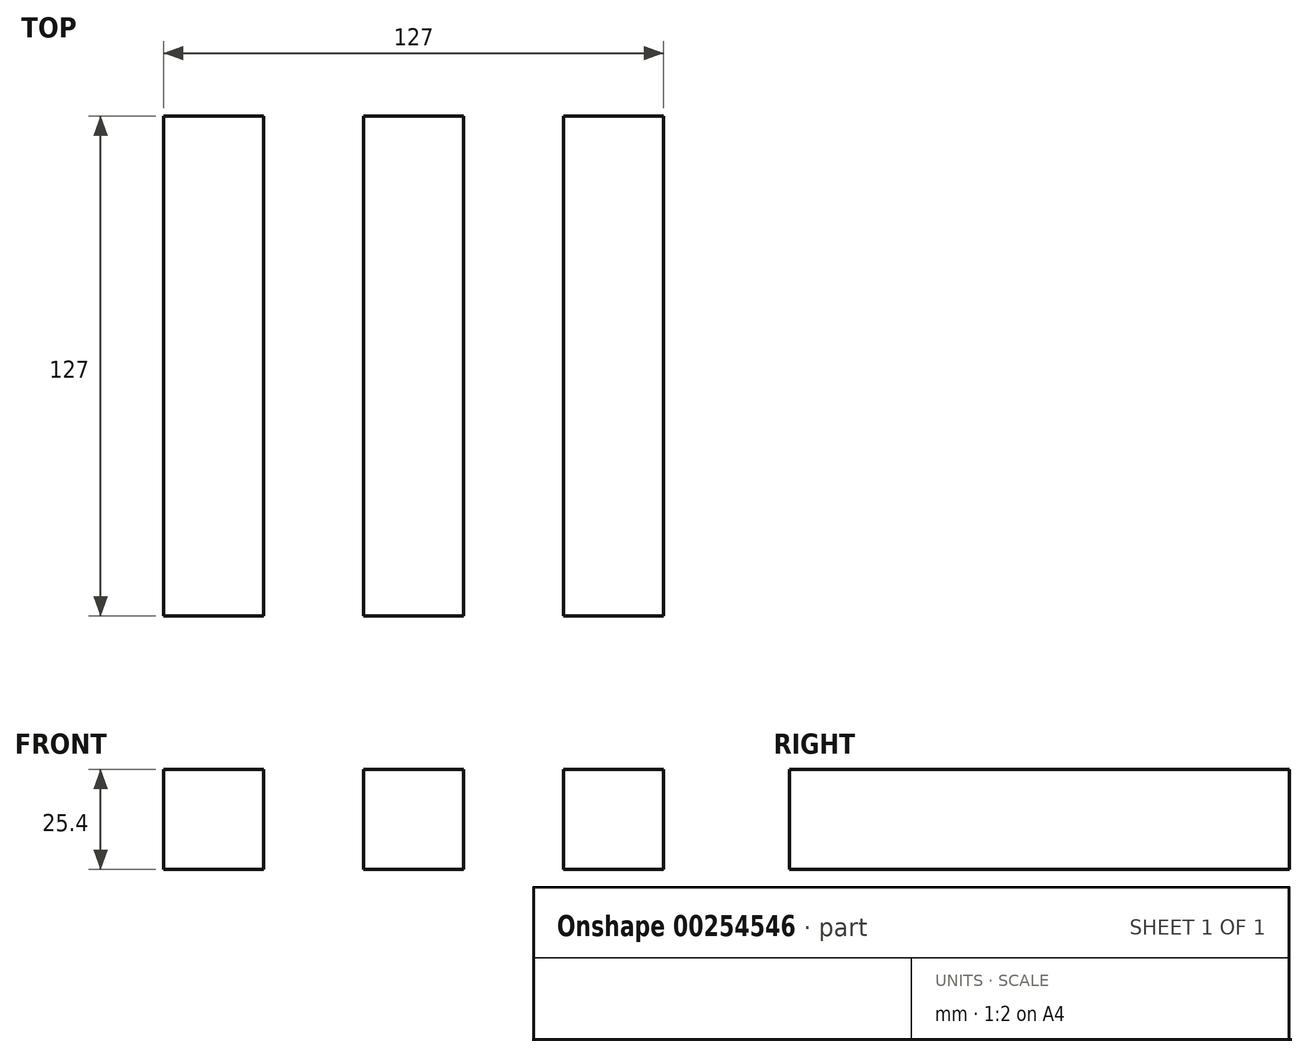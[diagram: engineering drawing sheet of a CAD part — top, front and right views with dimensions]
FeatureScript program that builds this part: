
annotation { "Feature Type Name" : "Feature", "Feature Type Description" : "" }
export const myFeature = defineFeature(function(context is Context, id is Id, definition is map)
    precondition{}
    {
        {
            var Q0;
            Q0=qCreatedBy(makeId("Front.planeOp"),FACE);
            var sketch = newSketch(context, id + "F0", { "sketchPlane" : qUnion([Q0])});
            skLineSegment(sketch, "E0.bottom", {"start": v(-49.45, -9.01) * mm, "end": v(-74.85, -9.01) * mm});
            skLineSegment(sketch, "E0.top", {"start": v(-49.45, 16.39) * mm, "end": v(-74.85, 16.39) * mm});
            skLineSegment(sketch, "E0.left", {"start": v(-49.45, -9.01) * mm, "end": v(-49.45, 16.39) * mm});
            skLineSegment(sketch, "E0.right", {"start": v(-74.85, -9.01) * mm, "end": v(-74.85, 16.39) * mm});
            skPoint(sketch, "E0.middle", {"position": v(-62.15, 3.69) * mm});
            skPoint(sketch, "E1.endSnap0", {"position": v(-49.45, 3.69) * mm});
            skLineSegment(sketch, "E2.bottom", {"start": v(1.35, -9.01) * mm, "end": v(-24.05, -9.01) * mm});
            skLineSegment(sketch, "E2.top", {"start": v(1.35, 16.39) * mm, "end": v(-24.05, 16.39) * mm});
            skLineSegment(sketch, "E2.left", {"start": v(1.35, -9.01) * mm, "end": v(1.35, 16.39) * mm});
            skLineSegment(sketch, "E2.right", {"start": v(-24.05, -9.01) * mm, "end": v(-24.05, 16.39) * mm});
            skPoint(sketch, "E2.middle", {"position": v(-11.35, 3.69) * mm});
            skLineSegment(sketch, "E3", {"start": v(-11.35, 3.69) * mm, "end": v(39.45, 3.69) * mm});
            skLineSegment(sketch, "E4.bottom", {"start": v(52.15, -9.01) * mm, "end": v(26.75, -9.01) * mm});
            skLineSegment(sketch, "E4.top", {"start": v(52.15, 16.39) * mm, "end": v(26.75, 16.39) * mm});
            skLineSegment(sketch, "E4.left", {"start": v(52.15, -9.01) * mm, "end": v(52.15, 16.39) * mm});
            skLineSegment(sketch, "E4.right", {"start": v(26.75, -9.01) * mm, "end": v(26.75, 16.39) * mm});
            skPoint(sketch, "E4.middle", {"position": v(39.45, 3.69) * mm});
            skLineSegment(sketch, "E5", {"start": v(-62.15, 3.69) * mm, "end": v(-11.35, 3.69) * mm});
            skSolve(sketch);
        }
        {
            var Q0;
            {var subQ3=sQuery(id+"F0.wireOp",EDGE,"E0.bottom");Q0=makeQuery(id+"F0.imprint","IMPRINT",FACE,{"disambiguationData":[TD([[makeQuery(id+"F0.imprint","IMPRINT",EDGE,{"derivedFrom":subQ3}),-1.0]])]});}
            var Q1;
            {var subQ6=sQuery(id+"F0.wireOp",EDGE,"E2.top");Q1=makeQuery(id+"F0.imprint","IMPRINT",FACE,{"disambiguationData":[TD([[makeQuery(id+"F0.imprint","IMPRINT",EDGE,{"derivedFrom":subQ6}),1.0]])]});}
            var Q2;
            {var subQ6=sQuery(id+"F0.wireOp",EDGE,"E2.bottom");Q2=makeQuery(id+"F0.imprint","IMPRINT",FACE,{"disambiguationData":[TD([[makeQuery(id+"F0.imprint","IMPRINT",EDGE,{"derivedFrom":subQ6}),-1.0]])]});}
            var Q3;
            {var subQ1=sQuery(id+"F0.wireOp",EDGE,"E4.bottom");Q3=makeQuery(id+"F0.imprint","IMPRINT",FACE,{"disambiguationData":[TD([[makeQuery(id+"F0.imprint","IMPRINT",EDGE,{"derivedFrom":subQ1}),-1.0]])]});}
            extrude(context, id + "F1", {"entities" : qUnion([Q0, Q1, Q2, Q3]), "endBound" : BoundingType.SYMMETRIC, "depth" : 127 * mm});
        }
    });
